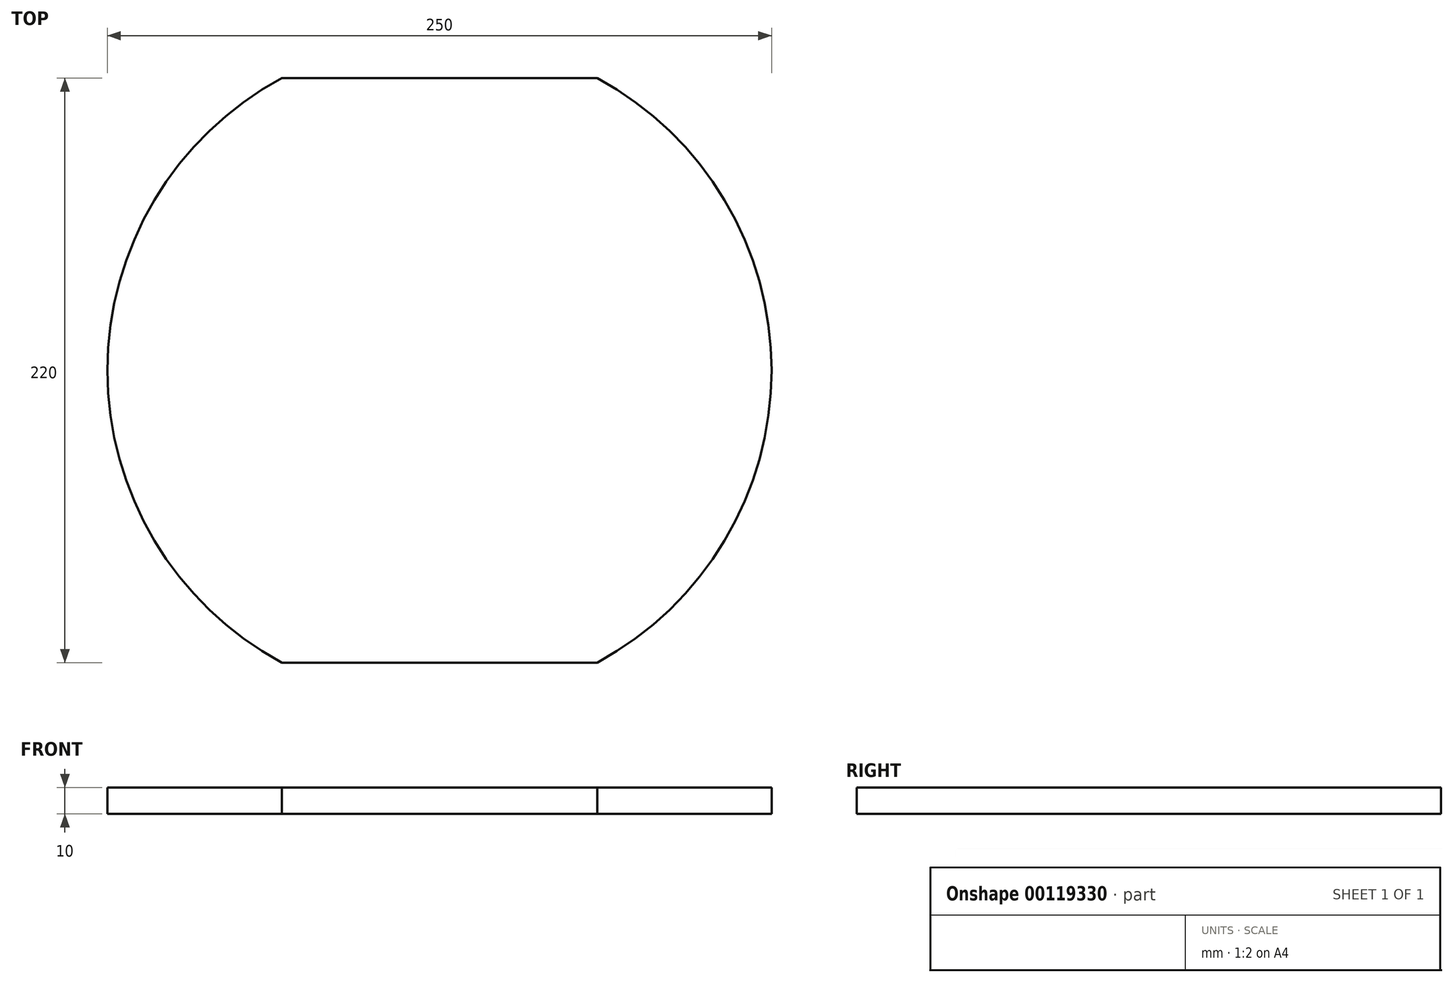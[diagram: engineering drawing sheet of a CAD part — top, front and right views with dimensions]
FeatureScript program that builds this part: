
annotation { "Feature Type Name" : "Feature", "Feature Type Description" : "" }
export const myFeature = defineFeature(function(context is Context, id is Id, definition is map)
    precondition{}
    {
        {
            var Q0;
            Q0=qCreatedBy(makeId("Top.planeOp"),FACE);
            var sketch = newSketch(context, id + "F0", { "sketchPlane" : qUnion([Q0])});
            skArc(sketch, "E0", {"start": v(-147.82, 110) * mm, "mid": v(-213.44, 0) * mm, "end": v(-147.82, -110) * mm});
            skArc(sketch, "E1", {"start": v(-29.07, -110) * mm, "mid": v(36.56, 0) * mm, "end": v(-29.07, 110) * mm});
            skLineSegment(sketch, "E2", {"start": v(-147.82, 110) * mm, "end": v(-29.07, 110) * mm});
            skLineSegment(sketch, "E3", {"start": v(-147.82, -110) * mm, "end": v(-29.07, -110) * mm});
            skSolve(sketch);
        }
        {
            var Q0;
            Q0=makeQuery(id+"F0.imprint","IMPRINT",FACE,{"disambiguationData":[TD([[makeQuery(id+"F0.imprint","IMPRINT",EDGE,{"derivedFrom":sQuery(id+"F0.wireOp",EDGE,"E0")}),1.0]])]});
            extrude(context, id + "F1", {"entities" : qUnion([Q0]), "depth" : 10 * mm});
        }
    });
